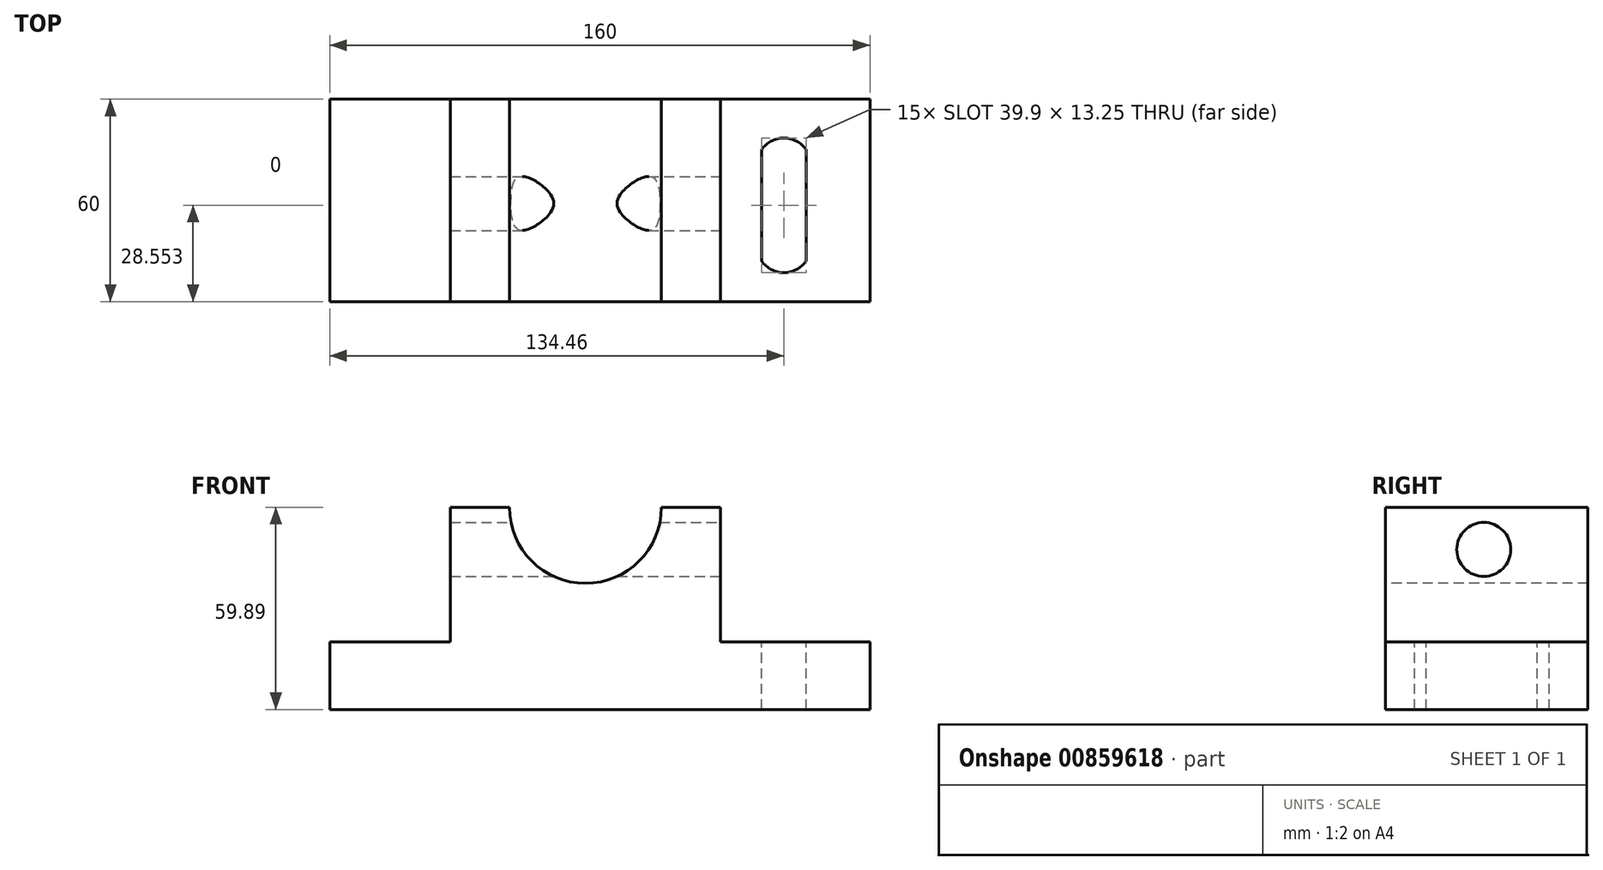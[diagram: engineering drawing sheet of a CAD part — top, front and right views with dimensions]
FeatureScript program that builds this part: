
annotation { "Feature Type Name" : "Feature", "Feature Type Description" : "" }
export const myFeature = defineFeature(function(context is Context, id is Id, definition is map)
    precondition{}
    {
        {
            var Q0;
            Q0=qCreatedBy(makeId("Front.planeOp"),FACE);
            var sketch = newSketch(context, id + "F0", { "sketchPlane" : qUnion([Q0])});
            skLineSegment(sketch, "E0.bottom", {"start": v(-75.7, -75.32) * mm, "end": v(84.3, -75.32) * mm});
            skLineSegment(sketch, "E0.top", {"start": v(-75.7, -55.32) * mm, "end": v(84.3, -55.32) * mm});
            skLineSegment(sketch, "E0.left", {"start": v(-75.7, -75.32) * mm, "end": v(-75.7, -55.32) * mm});
            skLineSegment(sketch, "E0.right", {"start": v(84.3, -75.32) * mm, "end": v(84.3, -55.32) * mm});
            skLineSegment(sketch, "E1.bottom", {"start": v(40, -15.43) * mm, "end": v(-40, -15.43) * mm});
            skLineSegment(sketch, "E1.left", {"start": v(40, -15.43) * mm, "end": v(40, -55.43) * mm});
            skLineSegment(sketch, "E1.right", {"start": v(-40, -15.43) * mm, "end": v(-40, -55.43) * mm});
            skPoint(sketch, "E1.middle", {"position": v(0, -35.43) * mm});
            skSolve(sketch);
        }
        {
            var Q0;
            {var subQ5=sQuery(id+"F0.wireOp",EDGE,"E1.bottom");Q0=makeQuery(id+"F0.imprint","IMPRINT",FACE,{"disambiguationData":[TD([[makeQuery(id+"F0.imprint","IMPRINT",EDGE,{"derivedFrom":subQ5}),1.0]])]});}
            var Q1;
            Q1=makeQuery(id+"F0.imprint","IMPRINT",FACE,{"disambiguationData":[TD([[makeQuery(id+"F0.imprint","IMPRINT",EDGE,{"derivedFrom":sQuery(id+"F0.wireOp",EDGE,"E0.bottom")}),1.0]])]});
            extrude(context, id + "F1", {"entities" : qUnion([Q0, Q1]), "depth" : 60 * mm, "offsetDistance" : 25 * mm});
        }
        {
            var Q0;
            Q0=makeQuery(id+"F1.opExtrude","CAP_FACE",FACE,{"disambiguationData":[OSD([sQuery(id+"F0.wireOp",EDGE,"E0.bottom"),sQuery(id+"F0.wireOp",EDGE,"E0.top"),sQuery(id+"F0.wireOp",EDGE,"E0.left"),sQuery(id+"F0.wireOp",EDGE,"E0.right"),sQuery(id+"F0.wireOp",EDGE,"E1.bottom"),sQuery(id+"F0.wireOp",EDGE,"E1.left"),sQuery(id+"F0.wireOp",EDGE,"E1.right")])],"isStart":false});
            var sketch = newSketch(context, id + "F2", { "sketchPlane" : qUnion([Q0])});
            skCircle(sketch, "E2", {"center": v(0, -15.43) * mm, "radius": 22.5 * mm});
            skSolve(sketch);
        }
        {
            var Q0;
            {var subQ0=sQuery(id+"F2.wireOp",EDGE,"E2");var subQ1=makeQuery(id+"F1.opExtrude","CAP_EDGE",EDGE,{"disambiguationData":[OSD([sQuery(id+"F0.wireOp",EDGE,"E1.bottom")])],"isStart":false});var subQ2=makeQuery(id+"F2.imprint","INTERSECT",VERTEX,{"disambiguationData":[OD(0.0)],"derivedFrom":[subQ1,subQ0]});Q0=makeQuery(id+"F2.imprint","IMPRINT",FACE,{"disambiguationData":[TD([[makeQuery(id+"F2.imprint","IMPRINT",EDGE,{"disambiguationData":[TD([[subQ2,-1.0]])],"derivedFrom":subQ0}),1.0]])]});}
            var Q1;
            {var subQ0=sQuery(id+"F2.wireOp",EDGE,"E2");var subQ1=makeQuery(id+"F1.opExtrude","CAP_EDGE",EDGE,{"disambiguationData":[OSD([sQuery(id+"F0.wireOp",EDGE,"E1.bottom")])],"isStart":false});var subQ2=makeQuery(id+"F2.imprint","INTERSECT",VERTEX,{"disambiguationData":[OD(0.0)],"derivedFrom":[subQ1,subQ0]});Q1=makeQuery(id+"F2.imprint","IMPRINT",FACE,{"disambiguationData":[TD([[makeQuery(id+"F2.imprint","IMPRINT",EDGE,{"disambiguationData":[TD([[subQ2,1.0]])],"derivedFrom":subQ0}),1.0]])]});}
            extrude(context, id + "F3", {"entities" : qUnion([Q0, Q1]), "operationType" : NewBodyOperationType.REMOVE, "endBound" : BoundingType.THROUGH_ALL, "oppositeDirection" : true, "depth" : 25 * mm, "offsetDistance" : 25 * mm});
        }
        {
            var Q0;
            {var subQ0=sQuery(id+"F0.wireOp",EDGE,"E0.top");Q0=makeQuery(id+"F1.opExtrude","SWEPT_FACE",FACE,{"disambiguationData":[OSD([subQ0]),TDD([makeQuery(id+"F0.imprint","IMPRINT",EDGE,{"disambiguationData":[TD([[makeQuery(id+"F0.imprint","INTERSECT",VERTEX,{"derivedFrom":[subQ0,sQuery(id+"F0.wireOp",EDGE,"E0.right")]}),1.0]])],"derivedFrom":subQ0})])]});}
            var sketch = newSketch(context, id + "F4", { "sketchPlane" : qUnion([Q0])});
            skLineSegment(sketch, "E3.left", {"start": v(160.78, -20.2) * mm, "end": v(160.78, -16.52) * mm});
            skLineSegment(sketch, "E3.right", {"start": v(160.78, -16.52) * mm, "end": v(160.78, -9.67) * mm});
            skLineSegment(sketch, "E4.left", {"start": v(65.37, -15.01) * mm, "end": v(65.37, -47.88) * mm});
            skLineSegment(sketch, "E4.right", {"start": v(52.13, -15.01) * mm, "end": v(52.13, -47.88) * mm});
            skArc(sketch, "E5", {"start": v(65.37, -15.01) * mm, "mid": v(58.75, -11.5) * mm, "end": v(52.13, -15.01) * mm});
            skArc(sketch, "E6", {"start": v(52.13, -47.88) * mm, "mid": v(58.75, -51.4) * mm, "end": v(65.37, -47.88) * mm});
            skLineSegment(sketch, "E7.bottom", {"start": v(-57.87, -47.88) * mm, "end": v(-52.87, -47.88) * mm});
            skLineSegment(sketch, "E7.top", {"start": v(-57.87, -14.01) * mm, "end": v(-52.87, -14.01) * mm});
            skLineSegment(sketch, "E7.left", {"start": v(-57.87, -47.88) * mm, "end": v(-57.87, -14.01) * mm});
            skLineSegment(sketch, "E7.right", {"start": v(-52.87, -47.88) * mm, "end": v(-52.87, -14.01) * mm});
            skSolve(sketch);
        }
        {
            var Q0;
            Q0=makeQuery(id+"F4.imprint","IMPRINT",FACE,{"disambiguationData":[TD([[makeQuery(id+"F4.imprint","IMPRINT",EDGE,{"derivedFrom":sQuery(id+"F4.wireOp",EDGE,"E4.left")}),-1.0]])]});
            var Q1;
            Q1=makeQuery(id+"F4.imprint","IMPRINT",FACE,{"disambiguationData":[TD([[makeQuery(id+"F4.imprint","IMPRINT",EDGE,{"derivedFrom":sQuery(id+"F4.wireOp",EDGE,"uInDxJD7-zjPv-88au-wtxL-3K8dFF6gYyJH.left")}),-1.0]])]});
            extrude(context, id + "F5", {"entities" : qUnion([Q0, Q1]), "operationType" : NewBodyOperationType.REMOVE, "endBound" : BoundingType.THROUGH_ALL, "oppositeDirection" : true, "depth" : 25 * mm, "offsetDistance" : 25 * mm});
        }
        {
            var Q0;
            Q0=makeQuery(id+"F1.opExtrude","SWEPT_FACE",FACE,{"disambiguationData":[OSD([sQuery(id+"F0.wireOp",EDGE,"E1.left")])]});
            var sketch = newSketch(context, id + "F6", { "sketchPlane" : qUnion([Q0])});
            skCircle(sketch, "E8", {"center": v(-30.88, -27.89) * mm, "radius": 8 * mm});
            skSolve(sketch);
        }
        {
            var Q0;
            Q0=makeQuery(id+"F6.imprint","IMPRINT",FACE,{"disambiguationData":[TD([[makeQuery(id+"F6.imprint","IMPRINT",EDGE,{"derivedFrom":sQuery(id+"F6.wireOp",EDGE,"E8")}),1.0]])]});
            var Q1;
            Q1=sQuery(id+"F6.wireOp",EDGE,"E8");
            extrude(context, id + "F7", {"entities" : qUnion([Q0]), "operationType" : NewBodyOperationType.REMOVE, "surfaceEntities" : qUnion([Q1]), "endBound" : BoundingType.THROUGH_ALL, "oppositeDirection" : true, "depth" : 25 * mm, "offsetDistance" : 25 * mm});
        }
    });
